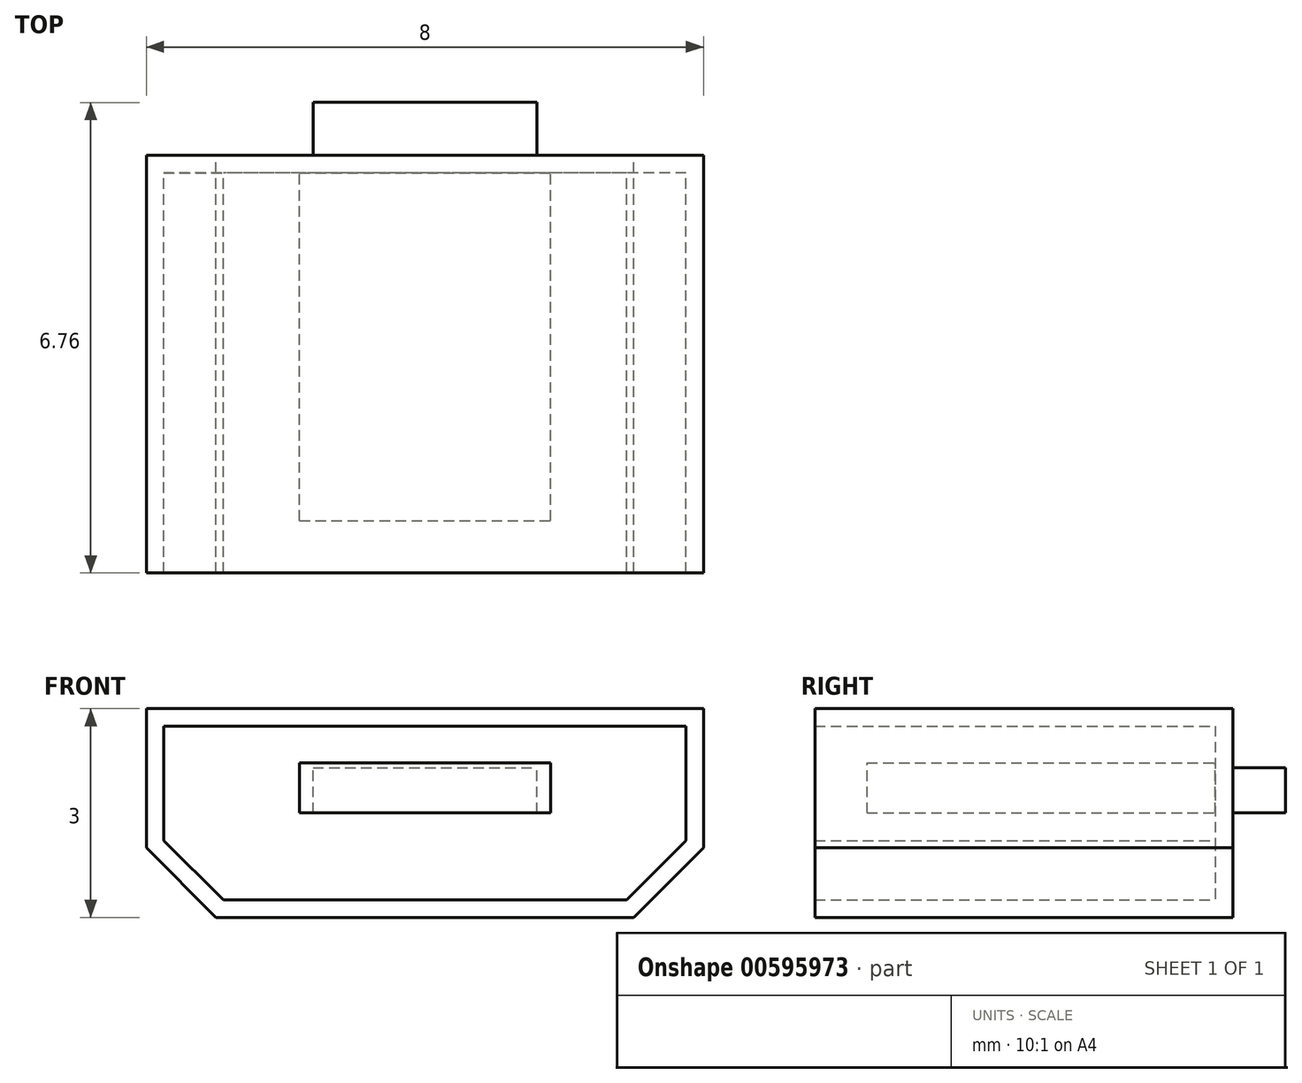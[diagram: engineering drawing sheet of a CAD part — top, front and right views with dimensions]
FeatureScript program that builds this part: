
annotation { "Feature Type Name" : "Feature", "Feature Type Description" : "" }
export const myFeature = defineFeature(function(context is Context, id is Id, definition is map)
    precondition{}
    {
        {
            var Q0;
            Q0=qCreatedBy(makeId("Front.planeOp"),FACE);
            var sketch = newSketch(context, id + "F0", { "sketchPlane" : qUnion([Q0])});
            skLineSegment(sketch, "E0.bottom", {"start": v(4, 1.5) * mm, "end": v(-4, 1.5) * mm});
            skLineSegment(sketch, "E0.top", {"start": v(4, -1.5) * mm, "end": v(-4, -1.5) * mm});
            skLineSegment(sketch, "E0.left", {"start": v(4, 1.5) * mm, "end": v(4, -1.5) * mm});
            skLineSegment(sketch, "E0.right", {"start": v(-4, 1.5) * mm, "end": v(-4, -1.5) * mm});
            skPoint(sketch, "E0.middle", {"position": v(0, 0) * mm});
            skLineSegment(sketch, "E1", {"start": v(-4, -0.5) * mm, "end": v(-3, -1.5) * mm});
            skLineSegment(sketch, "E2", {"start": v(-4, -0.5) * mm, "end": v(4, -0.5) * mm, "construction": true});
            skLineSegment(sketch, "E3", {"start": v(4, -0.5) * mm, "end": v(3, -1.5) * mm});
            skSolve(sketch);
        }
        {
            var Q0;
            {var subQ1=sQuery(id+"F0.wireOp",EDGE,"E0.bottom");Q0=makeQuery(id+"F0.imprint","IMPRINT",FACE,{"disambiguationData":[TD([[makeQuery(id+"F0.imprint","IMPRINT",EDGE,{"derivedFrom":subQ1}),1.0]])]});}
            extrude(context, id + "F1", {"entities" : qUnion([Q0]), "depth" : 6 * mm, "offsetDistance" : 25.4 * mm});
        }
        {
            var Q0;
            Q0=makeQuery(id+"F1.opExtrude","CAP_FACE",FACE,{"disambiguationData":[OSD([sQuery(id+"F0.wireOp",EDGE,"E0.bottom"),sQuery(id+"F0.wireOp",EDGE,"E0.top"),sQuery(id+"F0.wireOp",EDGE,"E0.left"),sQuery(id+"F0.wireOp",EDGE,"E0.right"),sQuery(id+"F0.wireOp",EDGE,"ENZDnjQn-iUoY-s3Z9-nI0O-kcBmxvAaHe41"),sQuery(id+"F0.wireOp",EDGE,"52y8hF0z-CPim-fXxM-H9yG-7wiXrCGiWtbV")])],"isStart":false});
            shell(context, id + "F2", {"entities" : qUnion([Q0]), "thickness" : 0.25 * mm});
        }
        {
            var Q0;
            Q0=makeQuery(id+"F2.opShell","OFFSET_FACE",FACE,{"disambiguationData":[OSD([sQuery(id+"F0.wireOp",EDGE,"E0.bottom"),sQuery(id+"F0.wireOp",EDGE,"E0.top"),sQuery(id+"F0.wireOp",EDGE,"E0.left"),sQuery(id+"F0.wireOp",EDGE,"E0.right"),sQuery(id+"F0.wireOp",EDGE,"ENZDnjQn-iUoY-s3Z9-nI0O-kcBmxvAaHe41"),sQuery(id+"F0.wireOp",EDGE,"52y8hF0z-CPim-fXxM-H9yG-7wiXrCGiWtbV")])]});
            var sketch = newSketch(context, id + "F3", { "sketchPlane" : qUnion([Q0])});
            skLineSegment(sketch, "E4.bottom", {"start": v(-1.8, 0) * mm, "end": v(0, 0) * mm});
            skLineSegment(sketch, "E4.top", {"start": v(-1.8, 0.72) * mm, "end": v(0, 0.72) * mm});
            skLineSegment(sketch, "E4.left", {"start": v(-1.8, 0) * mm, "end": v(-1.8, 0.72) * mm});
            skLineSegment(sketch, "E4.right", {"start": v(0, 0) * mm, "end": v(0, 0.72) * mm});
            skLineSegment(sketch, "E5.MirrorCS", {"start": v(1.8, 0.72) * mm, "end": v(0, 0.72) * mm});
            skLineSegment(sketch, "E6.MirrorCS", {"start": v(1.8, 0) * mm, "end": v(1.8, 0.72) * mm});
            skLineSegment(sketch, "E7.MirrorCS", {"start": v(1.8, 0) * mm, "end": v(0, 0) * mm});
            skSolve(sketch);
        }
        {
            var Q0;
            Q0=makeQuery(id+"F3.imprint","IMPRINT",FACE,{"disambiguationData":[TD([[makeQuery(id+"F3.imprint","IMPRINT",EDGE,{"derivedFrom":sQuery(id+"F3.wireOp",EDGE,"E4.bottom")}),1.0]])]});
            var Q1;
            Q1=makeQuery(id+"F3.imprint","IMPRINT",FACE,{"disambiguationData":[TD([[makeQuery(id+"F3.imprint","IMPRINT",EDGE,{"derivedFrom":sQuery(id+"F3.wireOp",EDGE,"E4.right")}),-1.0]])]});
            extrude(context, id + "F4", {"entities" : qUnion([Q0, Q1]), "operationType" : NewBodyOperationType.ADD, "depth" : 5 * mm, "offsetDistance" : 25.4 * mm});
        }
        {
            var Q0;
            Q0=makeQuery(id+"F1.opExtrude","CAP_FACE",FACE,{"disambiguationData":[OSD([sQuery(id+"F0.wireOp",EDGE,"E0.bottom"),sQuery(id+"F0.wireOp",EDGE,"E0.top"),sQuery(id+"F0.wireOp",EDGE,"E0.left"),sQuery(id+"F0.wireOp",EDGE,"E0.right"),sQuery(id+"F0.wireOp",EDGE,"ENZDnjQn-iUoY-s3Z9-nI0O-kcBmxvAaHe41"),sQuery(id+"F0.wireOp",EDGE,"52y8hF0z-CPim-fXxM-H9yG-7wiXrCGiWtbV")])],"isStart":true});
            var sketch = newSketch(context, id + "F5", { "sketchPlane" : qUnion([Q0])});
            skLineSegment(sketch, "E8.bottom", {"start": v(-1.6, 0) * mm, "end": v(0, 0) * mm});
            skLineSegment(sketch, "E8.top", {"start": v(-1.6, 0.65) * mm, "end": v(0, 0.65) * mm});
            skLineSegment(sketch, "E8.left", {"start": v(-1.6, 0) * mm, "end": v(-1.6, 0.65) * mm});
            skLineSegment(sketch, "E8.right", {"start": v(0, 0) * mm, "end": v(0, 0.65) * mm});
            skLineSegment(sketch, "E9.MirrorCS", {"start": v(1.6, 0.65) * mm, "end": v(0, 0.65) * mm});
            skLineSegment(sketch, "E10.MirrorCS", {"start": v(1.6, 0) * mm, "end": v(1.6, 0.65) * mm});
            skLineSegment(sketch, "E11.MirrorCS", {"start": v(1.6, 0) * mm, "end": v(0, 0) * mm});
            skSolve(sketch);
        }
        {
            var Q0;
            Q0=makeQuery(id+"F5.imprint","IMPRINT",FACE,{"disambiguationData":[TD([[makeQuery(id+"F5.imprint","IMPRINT",EDGE,{"derivedFrom":sQuery(id+"F5.wireOp",EDGE,"E8.right")}),-1.0]])]});
            var Q1;
            Q1=makeQuery(id+"F5.imprint","IMPRINT",FACE,{"disambiguationData":[TD([[makeQuery(id+"F5.imprint","IMPRINT",EDGE,{"derivedFrom":sQuery(id+"F5.wireOp",EDGE,"E8.bottom")}),1.0]])]});
            extrude(context, id + "F6", {"entities" : qUnion([Q0, Q1]), "operationType" : NewBodyOperationType.ADD, "depth" : 0.76 * mm, "offsetDistance" : 25.4 * mm});
        }
    });
